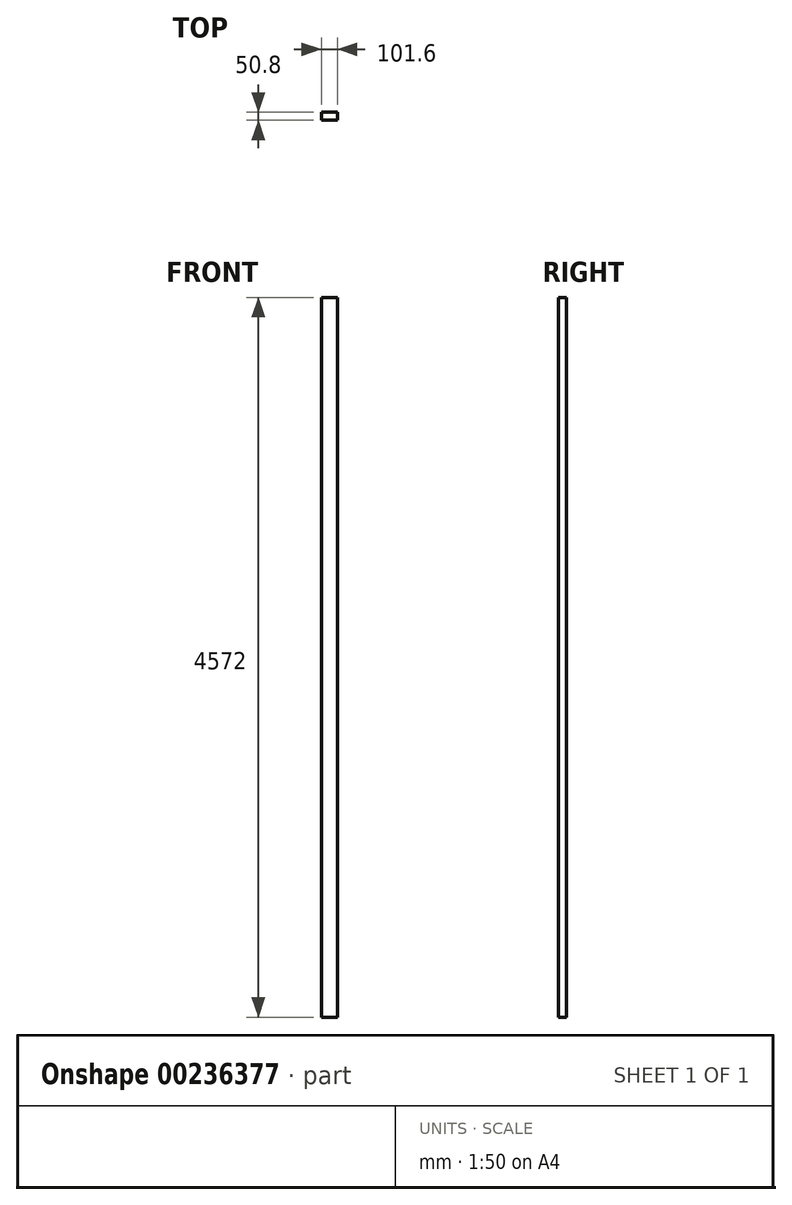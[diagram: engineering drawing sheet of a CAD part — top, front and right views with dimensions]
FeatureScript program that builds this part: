
annotation { "Feature Type Name" : "Feature", "Feature Type Description" : "" }
export const myFeature = defineFeature(function(context is Context, id is Id, definition is map)
    precondition{}
    {
        {
            var Q0;
            Q0=qCreatedBy(makeId("Front.planeOp"),FACE);
            var sketch = newSketch(context, id + "F0", { "sketchPlane" : qUnion([Q0])});
            skLineSegment(sketch, "E0.bottom", {"start": v(57.51, 4450.6) * mm, "end": v(-44.09, 4450.6) * mm});
            skLineSegment(sketch, "E0.top", {"start": v(57.51, -121.4) * mm, "end": v(-44.09, -121.4) * mm});
            skLineSegment(sketch, "E0.left", {"start": v(57.51, 4450.6) * mm, "end": v(57.51, -121.4) * mm});
            skLineSegment(sketch, "E0.right", {"start": v(-44.09, 4450.6) * mm, "end": v(-44.09, -121.4) * mm});
            skSolve(sketch);
        }
        {
            var Q0;
            Q0 = qSketchRegion(id + "F0", true);
            extrude(context, id + "F1", {"entities" : qUnion([Q0]), "depth" : 50.8 * mm});
        }
    });
